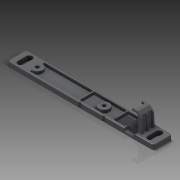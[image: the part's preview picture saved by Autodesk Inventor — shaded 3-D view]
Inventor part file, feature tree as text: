
AUTODESK INVENTOR PART (.ipt)
format: ipt  version: 2014 SP1 (Build 180222100, 222)  size: 388,096 bytes
history: native  units: in
note: dims shown in document units (in); Inventor stores cm internally (conversion verified against a paired STEP export)
features: fillet x1, imported_body x1
ambient origin geometry x8: Origin, YZ Plane, XZ Plane, XY Plane, X Axis, Y Axis, Z Axis, Center Point
bodies: Body1 (feature_tree)
feature tree (2):
  fillet  "Fillet8"  [1 undecoded]
  imported_body  "Base1"
note: 1 required parameter value undecoded (feature->parameter linkage not recoverable at this tier; creation-order binding heuristic only, values carry confidence <= 0.55)
